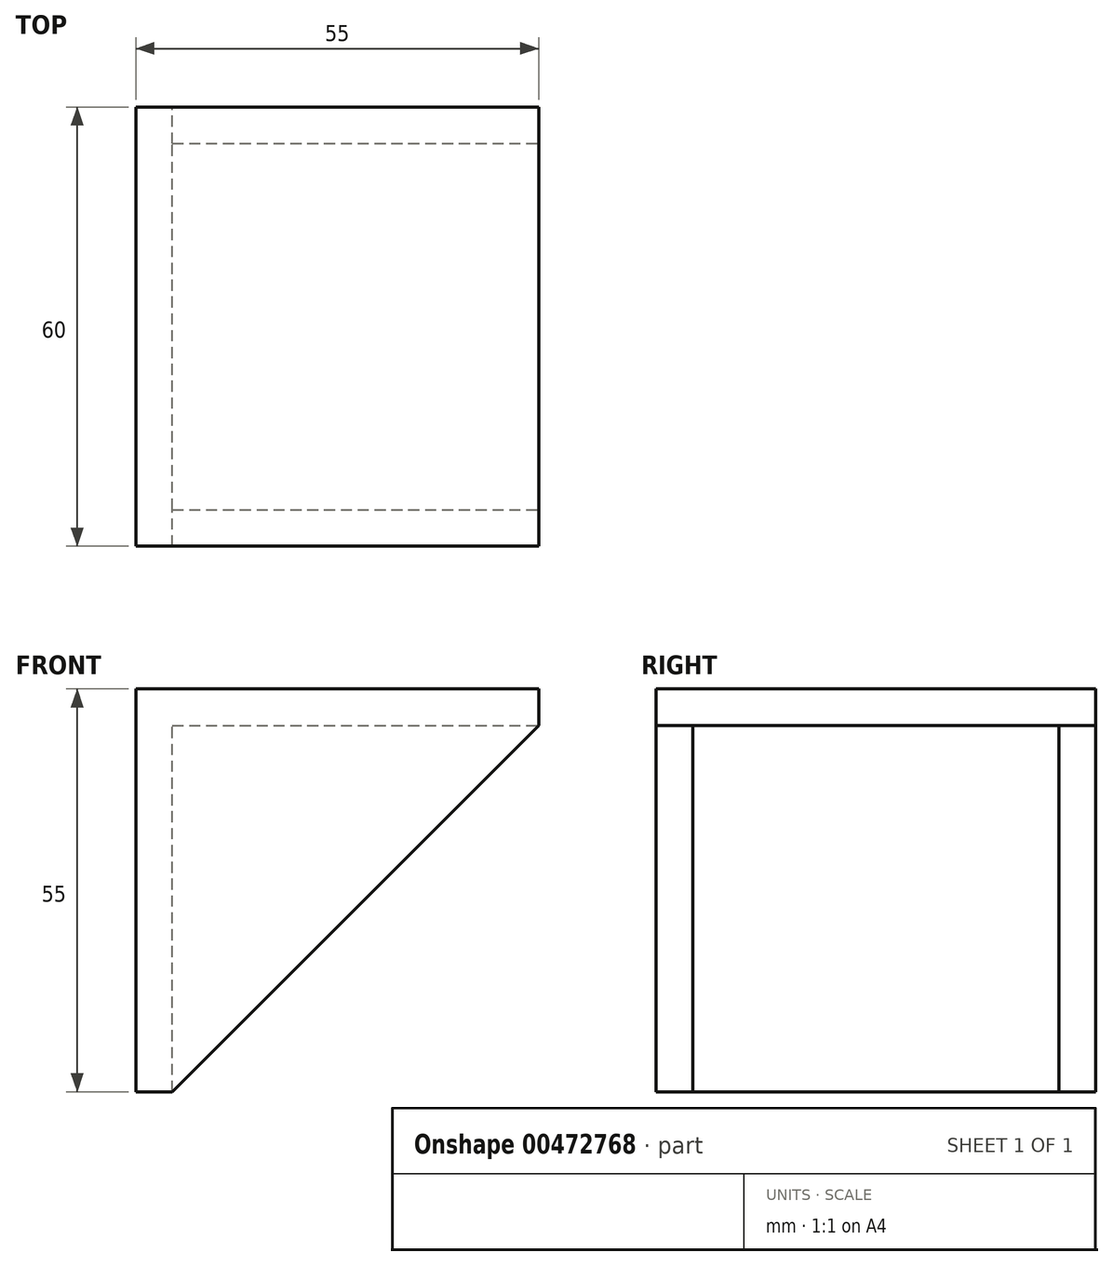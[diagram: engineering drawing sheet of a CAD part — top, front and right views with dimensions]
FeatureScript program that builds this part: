
annotation { "Feature Type Name" : "Feature", "Feature Type Description" : "" }
export const myFeature = defineFeature(function(context is Context, id is Id, definition is map)
    precondition{}
    {
        {
            assignVariable(context, id + "F0", {"name" : "W", "anyValue" : 50});
        }
        {
            assignVariable(context, id + "F1", {"name" : "eH", "anyValue" : 5});
        }
        {
            var Q0;
            Q0=qCreatedBy(makeId("Top.planeOp"),FACE);
            var sketch = newSketch(context, id + "F2", { "sketchPlane" : qUnion([Q0])});
            skLineSegment(sketch, "E0.bottom", {"start": v(-25, -25) * mm, "end": v(25, -25) * mm});
            skLineSegment(sketch, "E0.top", {"start": v(-25, 25) * mm, "end": v(25, 25) * mm});
            skLineSegment(sketch, "E0.left", {"start": v(-25, -25) * mm, "end": v(-25, 25) * mm});
            skLineSegment(sketch, "E0.right", {"start": v(25, -25) * mm, "end": v(25, 25) * mm});
            skPoint(sketch, "E0.middle", {"position": v(0, 0) * mm});
            skLineSegment(sketch, "E1.bottom", {"start": v(-25, -25) * mm, "end": v(-30, -25) * mm});
            skLineSegment(sketch, "E1.top", {"start": v(-25, 25) * mm, "end": v(-30, 25) * mm});
            skLineSegment(sketch, "E1.right", {"start": v(-30, -25) * mm, "end": v(-30, 25) * mm});
            skLineSegment(sketch, "E2.bottom", {"start": v(25, -25) * mm, "end": v(-30, -25) * mm});
            skLineSegment(sketch, "E2.top", {"start": v(25, -30) * mm, "end": v(-30, -30) * mm});
            skLineSegment(sketch, "E2.left", {"start": v(25, -25) * mm, "end": v(25, -30) * mm});
            skLineSegment(sketch, "E2.right", {"start": v(-30, -25) * mm, "end": v(-30, -30) * mm});
            skLineSegment(sketch, "E3.bottom", {"start": v(25, 25) * mm, "end": v(-30, 25) * mm});
            skLineSegment(sketch, "E3.top", {"start": v(25, 30) * mm, "end": v(-30, 30) * mm});
            skLineSegment(sketch, "E3.left", {"start": v(25, 25) * mm, "end": v(25, 30) * mm});
            skLineSegment(sketch, "E3.right", {"start": v(-30, 25) * mm, "end": v(-30, 30) * mm});
            skSolve(sketch);
        }
        {
            var Q0;
            Q0=makeQuery(id+"F2.imprint","IMPRINT",FACE,{"disambiguationData":[TD([[makeQuery(id+"F2.imprint","IMPRINT",EDGE,{"derivedFrom":sQuery(id+"F2.wireOp",EDGE,"E3.top")}),1.0]])]});
            var Q1;
            {var subQ0=sQuery(id+"F2.wireOp",EDGE,"E0.left");Q1=makeQuery(id+"F2.imprint","IMPRINT",FACE,{"disambiguationData":[TD([[makeQuery(id+"F2.imprint","IMPRINT",EDGE,{"derivedFrom":subQ0}),1.0]])]});}
            var Q2;
            {var subQ0=sQuery(id+"F2.wireOp",EDGE,"E0.right");Q2=makeQuery(id+"F2.imprint","IMPRINT",FACE,{"disambiguationData":[TD([[makeQuery(id+"F2.imprint","IMPRINT",EDGE,{"derivedFrom":subQ0}),1.0]])]});}
            var Q3;
            Q3=makeQuery(id+"F2.imprint","IMPRINT",FACE,{"disambiguationData":[TD([[makeQuery(id+"F2.imprint","IMPRINT",EDGE,{"derivedFrom":sQuery(id+"F2.wireOp",EDGE,"E2.top")}),-1.0]])]});
            extrude(context, id + "F3", {"entities" : qUnion([Q0, Q1, Q2, Q3]), "depth" : (getVariable(context, 'eH')) * mm, "offsetDistance" : 25 * mm});
        }
        {
            var Q0;
            Q0=makeQuery(id+"F2.imprint","IMPRINT",FACE,{"disambiguationData":[TD([[makeQuery(id+"F2.imprint","IMPRINT",EDGE,{"derivedFrom":sQuery(id+"F2.wireOp",EDGE,"E2.top")}),-1.0]])]});
            var Q1;
            Q1=makeQuery(id+"F2.imprint","IMPRINT",FACE,{"disambiguationData":[TD([[makeQuery(id+"F2.imprint","IMPRINT",EDGE,{"derivedFrom":sQuery(id+"F2.wireOp",EDGE,"E3.top")}),1.0]])]});
            var Q2;
            {var subQ0=sQuery(id+"F2.wireOp",EDGE,"E0.left");Q2=makeQuery(id+"F2.imprint","IMPRINT",FACE,{"disambiguationData":[TD([[makeQuery(id+"F2.imprint","IMPRINT",EDGE,{"derivedFrom":subQ0}),1.0]])]});}
            extrude(context, id + "F4", {"entities" : qUnion([Q0, Q1, Q2]), "operationType" : NewBodyOperationType.ADD, "oppositeDirection" : true, "depth" : (getVariable(context, 'W')) * mm, "offsetDistance" : 25 * mm});
        }
        {
            var Q0;
            {var subQ0=sQuery(id+"F2.wireOp",EDGE,"E3.top");Q0=makeQuery(id+"F4.boolean.opBoolean","MERGE",FACE,{"derivedFrom":[makeQuery(id+"F3.opExtrude","SWEPT_FACE",FACE,{"disambiguationData":[OSD([subQ0])]}),makeQuery(id+"F4.opExtrude","SWEPT_FACE",FACE,{"disambiguationData":[OSD([subQ0])]})]});}
            var sketch = newSketch(context, id + "F5", { "sketchPlane" : qUnion([Q0])});
            skLineSegment(sketch, "E4", {"start": v(-25, 5) * mm, "end": v(-25, 0) * mm});
            skLineSegment(sketch, "E5", {"start": v(-25, 0) * mm, "end": v(25, -50) * mm});
            skLineSegment(sketch, "E6", {"start": v(25, -50) * mm, "end": v(30, -50) * mm});
            skLineSegment(sketch, "E7", {"start": v(30, -50) * mm, "end": v(30, 5) * mm});
            skLineSegment(sketch, "E8", {"start": v(30, 5) * mm, "end": v(-25, 5) * mm});
            skLineSegment(sketch, "E9", {"start": v(25, -50) * mm, "end": v(-25, -50) * mm});
            skLineSegment(sketch, "E10", {"start": v(-25, -50) * mm, "end": v(-25, 0) * mm});
            skSolve(sketch);
        }
        {
            var Q0;
            Q0=makeQuery(id+"F5.imprint","IMPRINT",FACE,{"disambiguationData":[TD([[makeQuery(id+"F5.imprint","IMPRINT",EDGE,{"derivedFrom":sQuery(id+"F5.wireOp",EDGE,"E5")}),-1.0]])]});
            extrude(context, id + "F6", {"entities" : qUnion([Q0]), "operationType" : NewBodyOperationType.REMOVE, "endBound" : BoundingType.THROUGH_ALL, "oppositeDirection" : true, "depth" : 25 * mm, "offsetDistance" : 25 * mm});
        }
    });
